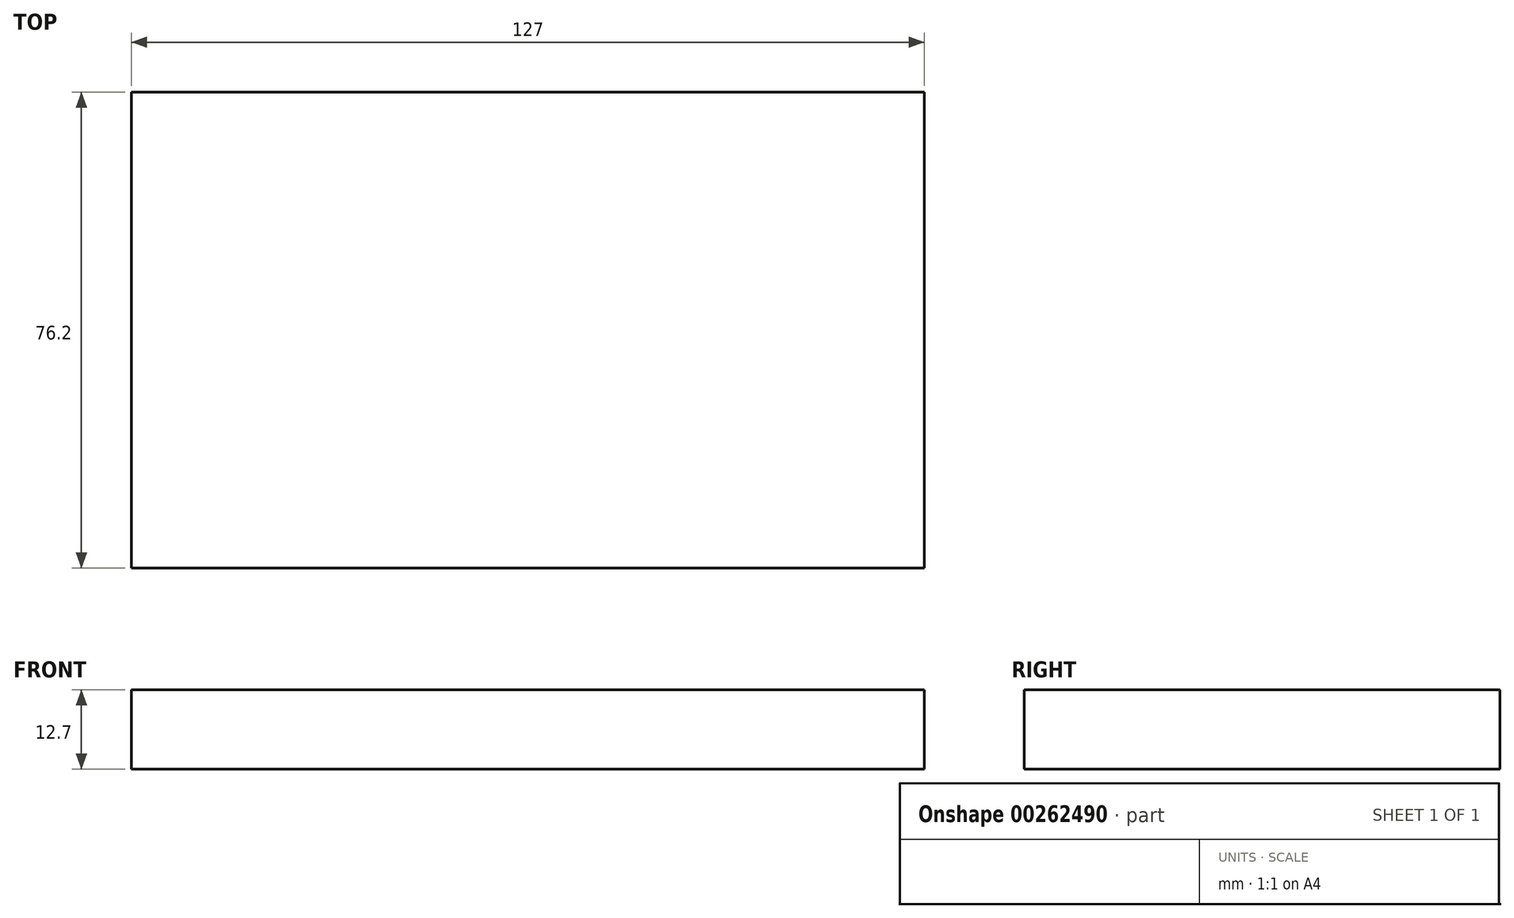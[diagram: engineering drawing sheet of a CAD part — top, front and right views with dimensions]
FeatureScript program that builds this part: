
annotation { "Feature Type Name" : "Feature", "Feature Type Description" : "" }
export const myFeature = defineFeature(function(context is Context, id is Id, definition is map)
    precondition{}
    {
        {
            var Q0;
            Q0=qCreatedBy(makeId("Top.planeOp"),FACE);
            var sketch = newSketch(context, id + "F0", { "sketchPlane" : qUnion([Q0])});
            skLineSegment(sketch, "E0.bottom", {"start": v(63.5, 38.1) * mm, "end": v(-63.5, 38.1) * mm});
            skLineSegment(sketch, "E0.top", {"start": v(63.5, -38.1) * mm, "end": v(-63.5, -38.1) * mm});
            skLineSegment(sketch, "E0.left", {"start": v(63.5, 38.1) * mm, "end": v(63.5, -38.1) * mm});
            skLineSegment(sketch, "E0.right", {"start": v(-63.5, 38.1) * mm, "end": v(-63.5, -38.1) * mm});
            skPoint(sketch, "E0.middle", {"position": v(0, 0) * mm});
            skPoint(sketch, "E1", {"position": v(44.45, 25.4) * mm});
            skSolve(sketch);
        }
        {
            var Q0;
            Q0 = qSketchRegion(id + "F0", true);
            extrude(context, id + "F1", {"entities" : qUnion([Q0]), "depth" : 12.7 * mm});
        }
    });
